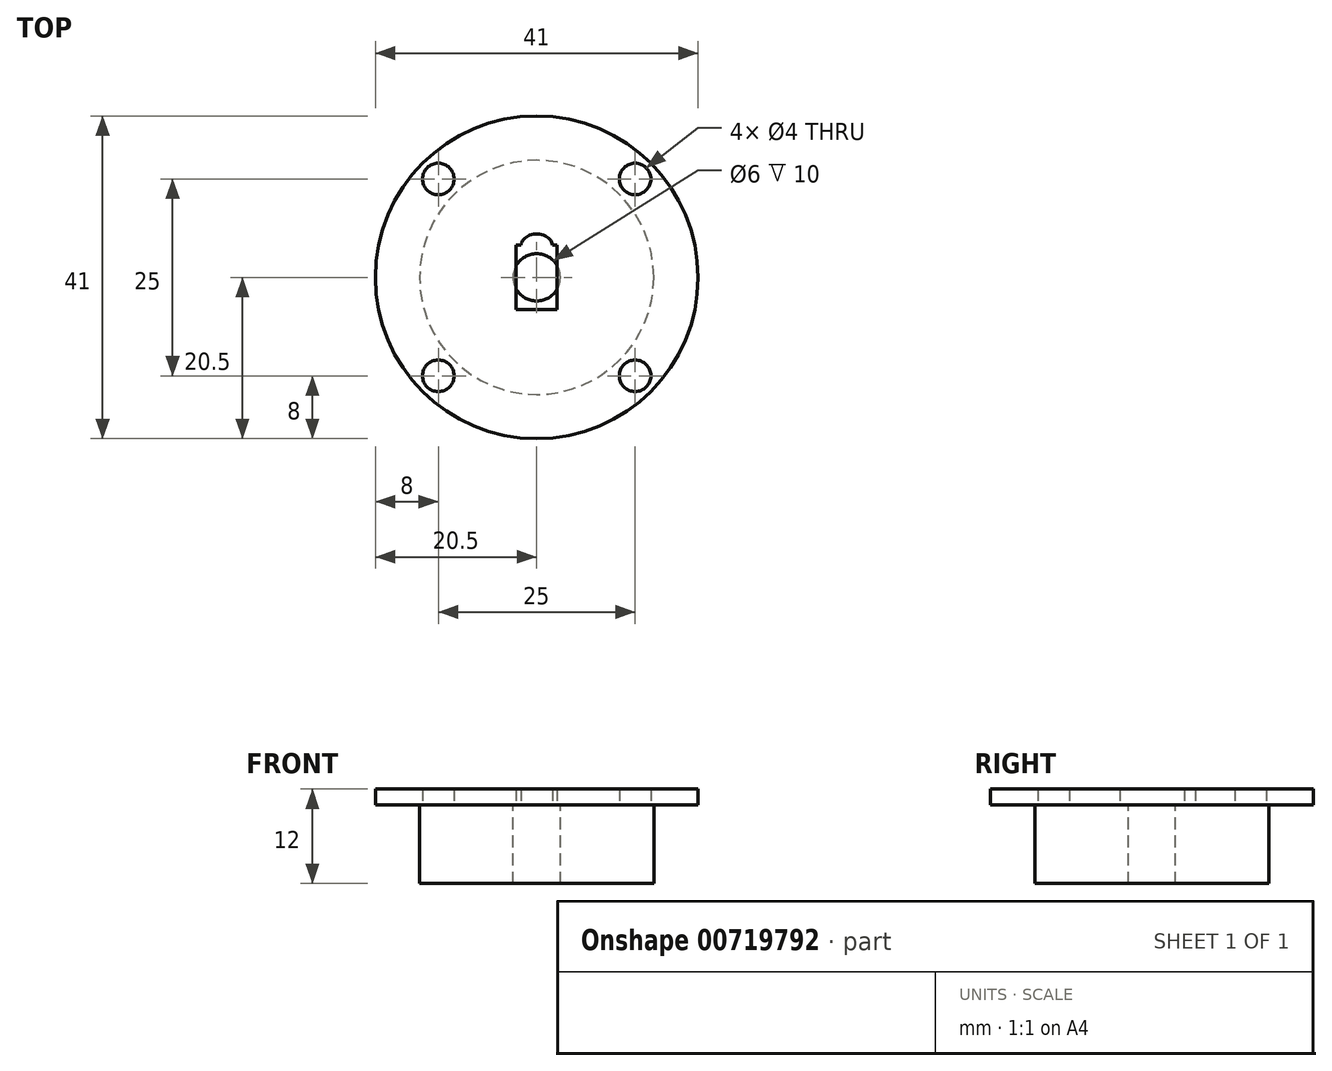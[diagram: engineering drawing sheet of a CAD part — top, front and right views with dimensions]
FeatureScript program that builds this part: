
annotation { "Feature Type Name" : "Feature", "Feature Type Description" : "" }
export const myFeature = defineFeature(function(context is Context, id is Id, definition is map)
    precondition{}
    {
        {
            var Q0;
            Q0=qCreatedBy(makeId("Top.planeOp"),FACE);
            var sketch = newSketch(context, id + "F0", { "sketchPlane" : qUnion([Q0])});
            skCircle(sketch, "E0", {"center": v(0, 0) * mm, "radius": 20.5 * mm});
            skSolve(sketch);
        }
        {
            var Q0;
            Q0 = qSketchRegion(id + "F0", true);
            extrude(context, id + "F1", {"entities" : qUnion([Q0]), "depth" : 2 * mm, "offsetDistance" : 25 * mm});
        }
        {
            var Q0;
            Q0=qCreatedBy(makeId("Top.planeOp"),FACE);
            var sketch = newSketch(context, id + "F2", { "sketchPlane" : qUnion([Q0])});
            skCircle(sketch, "E1", {"center": v(0, 0) * mm, "radius": 14.88 * mm});
            skSolve(sketch);
        }
        {
            var Q0;
            Q0 = qSketchRegion(id + "F2", true);
            extrude(context, id + "F3", {"entities" : qUnion([Q0]), "operationType" : NewBodyOperationType.ADD, "oppositeDirection" : true, "depth" : 10 * mm, "offsetDistance" : 25 * mm});
        }
        {
            var Q0;
            Q0=qCreatedBy(makeId("Top.planeOp"),FACE);
            var sketch = newSketch(context, id + "F4", { "sketchPlane" : qUnion([Q0])});
            skCircle(sketch, "E2", {"center": v(-12.5, 12.5) * mm, "radius": 2 * mm});
            skCircle(sketch, "E3", {"center": v(12.5, 12.5) * mm, "radius": 2 * mm});
            skCircle(sketch, "E4", {"center": v(12.5, -12.5) * mm, "radius": 2 * mm});
            skCircle(sketch, "E5", {"center": v(-12.5, -12.5) * mm, "radius": 2 * mm});
            skSolve(sketch);
        }
        {
            var Q0;
            Q0 = qSketchRegion(id + "F4", true);
            extrude(context, id + "F5", {"entities" : qUnion([Q0]), "operationType" : NewBodyOperationType.REMOVE, "depth" : 2 * mm, "offsetDistance" : 25 * mm});
        }
        {
            var Q0;
            Q0=qCreatedBy(makeId("Top.planeOp"),FACE);
            var sketch = newSketch(context, id + "F6", { "sketchPlane" : qUnion([Q0])});
            skCircle(sketch, "E6", {"center": v(0, 0) * mm, "radius": 3 * mm});
            skSolve(sketch);
        }
        {
            var Q0;
            Q0 = qSketchRegion(id + "F6", true);
            extrude(context, id + "F7", {"entities" : qUnion([Q0]), "operationType" : NewBodyOperationType.REMOVE, "oppositeDirection" : true, "depth" : 10 * mm, "offsetDistance" : 25 * mm});
        }
        {
            var Q0;
            Q0=qCreatedBy(makeId("Top.planeOp"),FACE);
            var sketch = newSketch(context, id + "F8", { "sketchPlane" : qUnion([Q0])});
            skLineSegment(sketch, "E7.bottom", {"start": v(2.6, -4.1) * mm, "end": v(-2.6, -4.1) * mm});
            skLineSegment(sketch, "E7.top", {"start": v(2.6, 4.1) * mm, "end": v(-2.6, 4.1) * mm});
            skLineSegment(sketch, "E7.left", {"start": v(2.6, -4.1) * mm, "end": v(2.6, 4.1) * mm});
            skLineSegment(sketch, "E7.right", {"start": v(-2.6, -4.1) * mm, "end": v(-2.6, 4.1) * mm});
            skPoint(sketch, "E7.middle", {"position": v(0, 0) * mm});
            skSolve(sketch);
        }
        {
            var Q0;
            Q0 = qSketchRegion(id + "F8", true);
            extrude(context, id + "F9", {"entities" : qUnion([Q0]), "operationType" : NewBodyOperationType.REMOVE, "depth" : 2 * mm, "offsetDistance" : 25 * mm});
        }
        {
            var Q0;
            Q0=qCreatedBy(makeId("Top.planeOp"),FACE);
            var sketch = newSketch(context, id + "F10", { "sketchPlane" : qUnion([Q0])});
            skEllipse(sketch, "E8", {"center": v(0, 4) * mm, "majorRadius": 2 * mm, "minorRadius": 1.5 * mm, "majorAxis": v(1, 0)});
            skSolve(sketch);
        }
        {
            var Q0;
            Q0=makeQuery(id+"F10.imprint","IMPRINT",FACE,{"disambiguationData":[TD([[makeQuery(id+"F10.imprint","IMPRINT",EDGE,{"derivedFrom":sQuery(id+"F10.wireOp",EDGE,"E8")}),1.0]])]});
            var Q1;
            Q1=sQuery(id+"F10.wireOp",EDGE,"E8");
            extrude(context, id + "F11", {"entities" : qUnion([Q0]), "operationType" : NewBodyOperationType.REMOVE, "surfaceEntities" : qUnion([Q1]), "depth" : 2 * mm, "offsetDistance" : 25 * mm});
        }
    });
